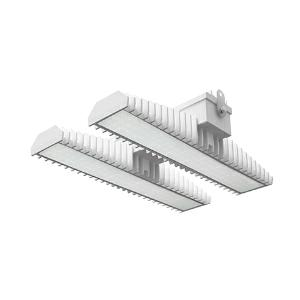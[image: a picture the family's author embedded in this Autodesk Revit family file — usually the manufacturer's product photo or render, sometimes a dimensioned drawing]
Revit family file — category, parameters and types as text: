
# Revit family: 3f_filippi_-_3f_lem_ampio_3f_filippi_-_59158_a0812_-_3f_lem_2_led_100-865_cr_ampio___vs_5824
name_source: partatom
category: Lighting Fixtures
units: mm (PartAtom-declared; Revit-internal decimal feet)

## family parameters
Cut with Voids When Loaded = No
Host = Face
Light Source = No
Part Type = Normal
Room Calculation Point = No
Round Connector Dimension = Use Diameter
Shared = No

## types (1)
- 3F Filippi - 3F LEM Ampio (1 x LED, 13304 lm, 109 W, 6500 K)
    Apparent Load = 109 VA
    Approval mark = CE
    CIE Flux Codes = 67 90 97 100 100
    Color Rendering = 80
    Color Temperature = 6500 K
    Control Gear = Electronic ballast
    Default Elevation = 1800 mm
    Description = Industrial luminaire with high light output and high luminous efficiency designed with the most innovative technologies for environments with temperature up to 55°C.

ILLUMINOTECHNICAL
Luminous efficiency 100% (DLOR 98%, ULOR 2%).
Initial luminous flux of the luminaire 13304 lm.
Direct symmetric wide distribution: the illuminated area has a rectangular shape.
Installation Interdistance Transv.D = 1.24 x hu - Long.D = 1.20 x hu.
Tabular UGR (CIE 117 - 4H-8H; S=0.25H; 70/50/20): RUG 22.1 - 22.2.
Beam angle: 82° - 83°.
Luminous efficacy 122 lm/W.
Lifetime (L93/B10): 30000 h. (tq+25°C)
Lifetime (L90/B10): 50000 h. (tq+25°C)
Lifetime (L85/B10): 80000 h. (tq+25°C)
Lifetime (L80/B10): 100000 h. (tq+25°C)
Lifetime (L85/B10): 50000 h. (tq+55°C)
Sudden decreased luminous flux after 50000 hours: 0% (C0).
Photobiological safety in compliance with IEC/TR 62778: RG0 risk exempt, (IEC 62471).
In compliance with IEC/EN 62722-2-1 - IEC/EN 62717 standards.

SOURCE
2 Mid-Power linear LED modules 50W/865.
Energy efficiency class (UE 2019/2020 - UE 2019/2015): C.
CIE 13.3 Colour rendering index: CRI >80 (R9 <50%).
IES TM-30 Fidelity Index: Rf = 84 Rg = 95.
CCT nominal colour temperature 6500 K.
Colour initial tolerance (MacAdam): SDCM 3.

MECHANICAL
Passive modular heatsinks in die-casted aluminium, painted in white colour.
To optimize the thermal management of the LED module, the heatsinks are oversized and provided with self-cleaning of cooling fins.
Wiring body in aluminium and galvanised steel anchored solidly to the sinks and thermally separated.
3F Lens lenses with high luminous efficiency, transparent methacrylate (PMMA), fixed to the LED modules.
Fixing brackets in stainless steel.
Luminaire with limited surface temperature. - D - (EN 60598-2-24)
Dimensions: 470x542 mm, height 133 mm. Weight 10.12 kg.
IP65 protection degree.
Mechanical strength to impacts IK06 (1 joule).
Glow-wire test resistance 650°C.

ELECTRICAL
Halogen Free electronic wiring 230V-50/60Hz, power factor 0.97, THD <25%, constant output current, class I, 1 driver.
Power of the luminaire 109 W.
ENEC - CE.
SAFE FLICKER: PstLM=<1 and SVM=<0.4 (IEC TR 61547-1 and IEC TR 63158), to ensure a more comfortable and safe light.
Luminaire compliant with EN 60598-2-22 for power supply from a centralised emergency system CPSS (Central Power Supply System), not incorporated in the luminaire - high risk areas excluded. The default power and flux are 100% in AC and 100% in DC.
Ambient temperature from -30°C to +55°C.
Temperature class T6 max 85°C.
Quick connection via M20 3P connector with 9-13 mm tightening range.
Power unit positioned on a separate compartment by the LED module to ensure optimum temperatures of cabling components, to be inspectable and maintainable.
Relative humidity UR: <85%.

INSTALLATION
Ceiling / Suspended / Wall.
All accessories dedicated to this product are available on the Catalog and on our website www.3F-Filippi.com.

ACCESSORIES
A0812 - Anti-glare microprismatic VS moulded glass, tempered, not flammable, with sealing gasket.
One required for each light module. The pack contains 10 pieces.

APPLICATIONS
In commercial environments, exhibition and industrial areas, stores, open areas.
Applications with high ambient temperature up to 55°C.
Environments in which it is necessary a total protection against falling fragments (eg environments with foodstuffs or machines with moving parts or with extreme temperature changes), use luminaires with polycarbonate lenses.

WARNING
Fixture not suitable for cold stores with an ambient temperature <0°C and/or relative humidity >85%.
Luminaire designed for disposal/recycling at end-of-life.
Replaceable (LED only) light source by a professional. Replaceable control gear by a professional.
    Height = 133 mm  [stored 0.436352 ft]
    Lamp = 1 x LED
    Lamp Light Flux = 13304 lm
    Lamp Power = 109 W
    Lamp count = 1
    Length = 470 mm
    Lifetime = 50000 h
    Luminous efficacy = 122 lm/W
    Manufacturer = 3F Filippi
    ModVariant = No
    Model = 3F Filippi - 59158+A0812 - 3F LEM 2 LED 100-865 CR AMPIO + VS
    Mounting Place = Ceiling
    Mounting Type = Pendant
    Number of Poles = 1
    OnlyDefault = Yes
    Power Factor = 1
    Product Name = 3F Filippi - 3F LEM Ampio
    Product group = pendant luminaire
    ProductGroupID = 9
    Protection Class = Protection class I
    Protection Degree = IP 65
    RLX_Detail_Level = 1
    RLX_Emergency_Light_Flux = 0 lm
    RLX_Emergency_Type = 0
    RLX_Emergency_Type_DB = No
    RlxData = <blob elided: 95205 chars, md5=6f986f37>
    Socket = socket
    Standby Power = 0 W
    System Light Flux = 13304 lm
    System Power = 109 W
    Type Comments = Product without accessories
    Type Image = 3f_filippi_-_lem_2__a0812.jpg
    URL = http://relux.com
    VarID = ---
    Voltage = 0 V
    Weight = 0.00 kg
    Width = 542 mm

note: [stored X ft] marks values corroborated as IEEE doubles in the binary element streams (Revit-internal decimal feet)

## geometry (parser evidence)
native form markers: Blend x4, Sweep x13
no freeform markers — native parametric forms only
